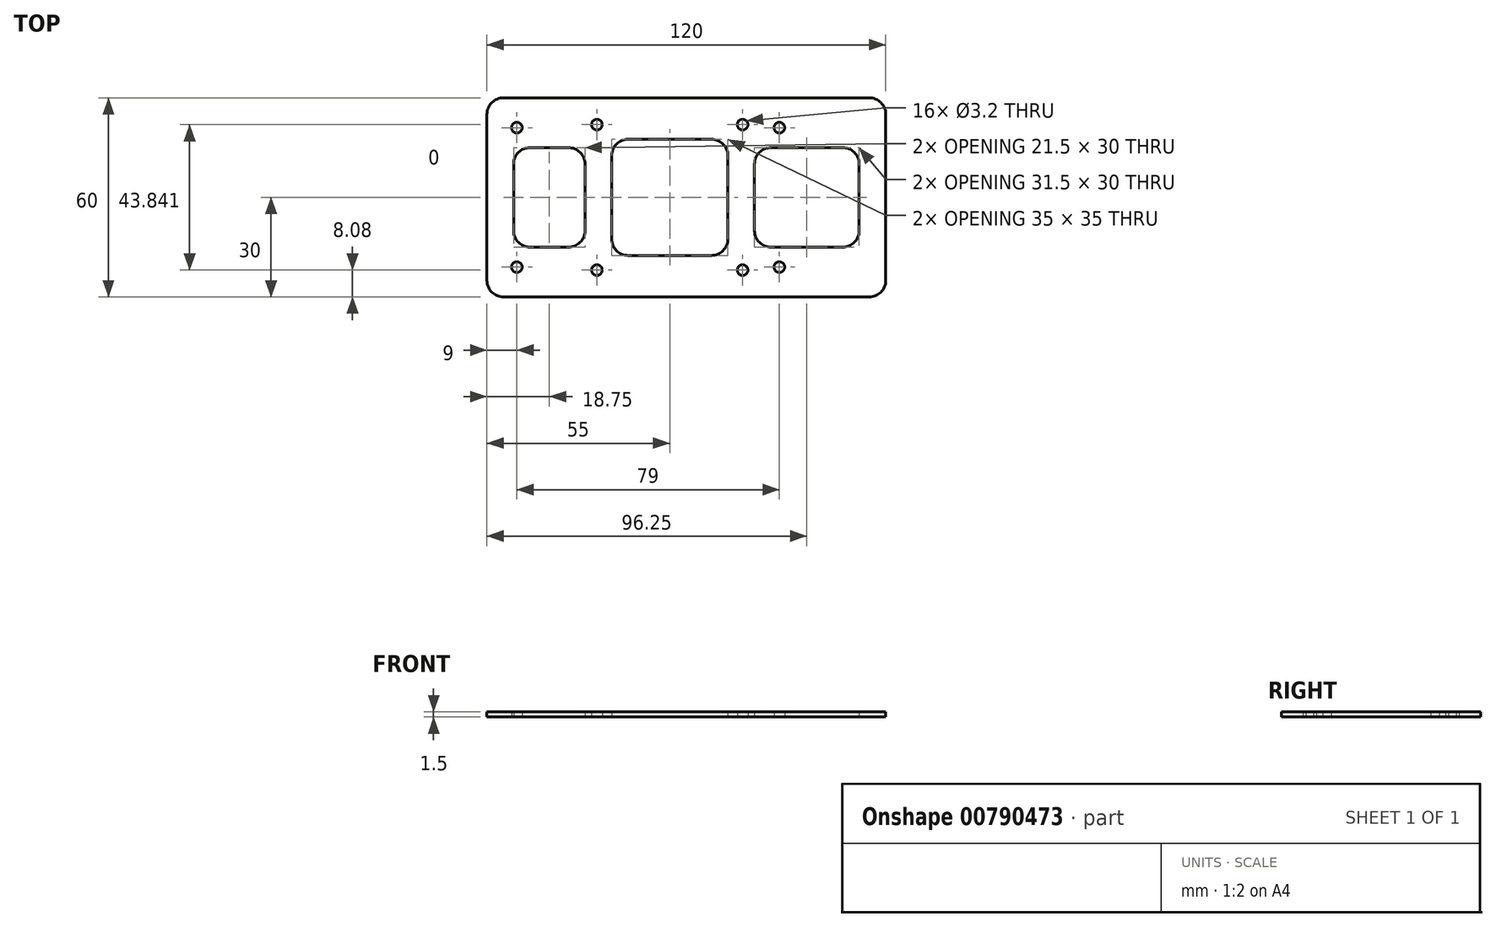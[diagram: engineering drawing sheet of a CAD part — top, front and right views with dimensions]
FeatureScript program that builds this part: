
annotation { "Feature Type Name" : "Feature", "Feature Type Description" : "" }
export const myFeature = defineFeature(function(context is Context, id is Id, definition is map)
    precondition{}
    {
        {
            var Q0;
            Q0=qCreatedBy(makeId("Top.planeOp"),FACE);
            var sketch = newSketch(context, id + "F0", { "sketchPlane" : qUnion([Q0])});
            skLineSegment(sketch, "E0.bottom", {"start": v(-60, 30) * mm, "end": v(60, 30) * mm});
            skLineSegment(sketch, "E0.top", {"start": v(-60, -30) * mm, "end": v(60, -30) * mm});
            skLineSegment(sketch, "E0.left", {"start": v(-60, 30) * mm, "end": v(-60, -30) * mm});
            skLineSegment(sketch, "E0.right", {"start": v(60, 30) * mm, "end": v(60, -30) * mm});
            skLineSegment(sketch, "E1.bottom", {"start": v(-51, 21) * mm, "end": v(28, 21) * mm, "construction": true});
            skLineSegment(sketch, "E1.top", {"start": v(-51, -21) * mm, "end": v(28, -21) * mm, "construction": true});
            skLineSegment(sketch, "E1.left", {"start": v(-51, 21) * mm, "end": v(-51, -21) * mm, "construction": true});
            skLineSegment(sketch, "E1.right", {"start": v(28, 21) * mm, "end": v(28, -21) * mm, "construction": true});
            skCircle(sketch, "E2", {"center": v(-51, 21) * mm, "radius": 1.6 * mm});
            skCircle(sketch, "E3", {"center": v(28, 21) * mm, "radius": 1.6 * mm});
            skCircle(sketch, "E4", {"center": v(-51, -21) * mm, "radius": 1.6 * mm});
            skCircle(sketch, "E5", {"center": v(28, -21) * mm, "radius": 1.6 * mm});
            skLineSegment(sketch, "E6.bottom", {"start": v(-26.92, 21.92) * mm, "end": v(16.92, 21.92) * mm, "construction": true});
            skLineSegment(sketch, "E6.top", {"start": v(-26.92, -21.92) * mm, "end": v(16.92, -21.92) * mm, "construction": true});
            skLineSegment(sketch, "E6.left", {"start": v(-26.92, 21.92) * mm, "end": v(-26.92, -21.92) * mm, "construction": true});
            skLineSegment(sketch, "E6.right", {"start": v(16.92, 21.92) * mm, "end": v(16.92, -21.92) * mm, "construction": true});
            skLineSegment(sketch, "E7", {"start": v(-26.92, -21.92) * mm, "end": v(16.92, 21.92) * mm, "construction": true});
            skCircle(sketch, "E8", {"center": v(16.92, 21.92) * mm, "radius": 1.6 * mm});
            skCircle(sketch, "E9", {"center": v(-26.92, 21.92) * mm, "radius": 1.6 * mm});
            skCircle(sketch, "E10", {"center": v(-26.92, -21.92) * mm, "radius": 1.6 * mm});
            skCircle(sketch, "E11", {"center": v(16.92, -21.92) * mm, "radius": 1.6 * mm});
            skLineSegment(sketch, "E12", {"start": v(-26.92, 21.92) * mm, "end": v(16.92, -21.92) * mm, "construction": true});
            skPoint(sketch, "E13", {"position": v(-5, 0) * mm});
            skLineSegment(sketch, "E14.bottom", {"start": v(-55, 25) * mm, "end": v(54.5, 25) * mm, "construction": true});
            skLineSegment(sketch, "E14.top", {"start": v(-55, -25) * mm, "end": v(54.5, -25) * mm, "construction": true});
            skLineSegment(sketch, "E14.left", {"start": v(-55, 25) * mm, "end": v(-55, -25) * mm, "construction": true});
            skLineSegment(sketch, "E14.right", {"start": v(54.5, 25) * mm, "end": v(54.5, -25) * mm, "construction": true});
            skLineSegment(sketch, "E15.bottom", {"start": v(-22.5, 17.5) * mm, "end": v(12.5, 17.5) * mm});
            skLineSegment(sketch, "E15.top", {"start": v(-22.5, -17.5) * mm, "end": v(12.5, -17.5) * mm});
            skLineSegment(sketch, "E15.left", {"start": v(-22.5, 17.5) * mm, "end": v(-22.5, -17.5) * mm});
            skLineSegment(sketch, "E15.right", {"start": v(12.5, 17.5) * mm, "end": v(12.5, -17.5) * mm});
            skLineSegment(sketch, "E16.bottom", {"start": v(52, -15) * mm, "end": v(20.5, -15) * mm});
            skLineSegment(sketch, "E16.top", {"start": v(52, 15) * mm, "end": v(20.5, 15) * mm});
            skLineSegment(sketch, "E16.left", {"start": v(52, -15) * mm, "end": v(52, 15) * mm});
            skLineSegment(sketch, "E16.right", {"start": v(20.5, -15) * mm, "end": v(20.5, 15) * mm});
            skPoint(sketch, "E16.middle", {"position": v(36.25, 0) * mm});
            skLineSegment(sketch, "E17.bottom", {"start": v(-52, -15) * mm, "end": v(-30.5, -15) * mm});
            skLineSegment(sketch, "E17.top", {"start": v(-52, 15) * mm, "end": v(-30.5, 15) * mm});
            skLineSegment(sketch, "E17.left", {"start": v(-52, -15) * mm, "end": v(-52, 15) * mm});
            skLineSegment(sketch, "E17.right", {"start": v(-30.5, -15) * mm, "end": v(-30.5, 15) * mm});
            skPoint(sketch, "E17.middle", {"position": v(-41.25, 0) * mm});
            skSolve(sketch);
        }
        {
            var Q0;
            Q0=makeQuery(id+"F0.imprint","IMPRINT",FACE,{"disambiguationData":[TD([[makeQuery(id+"F0.imprint","IMPRINT",EDGE,{"derivedFrom":sQuery(id+"F0.wireOp",EDGE,"E0.bottom")}),-1.0]])]});
            extrude(context, id + "F1", {"entities" : qUnion([Q0]), "depth" : 1.5 * mm, "offsetDistance" : 25 * mm});
        }
        {
            var Q0;
            Q0=makeQuery(id+"F1.opExtrude","SWEPT_EDGE",EDGE,{"disambiguationData":[OSD([sQuery(id+"F0.wireOp",EDGE,"E0.bottom"),sQuery(id+"F0.wireOp",EDGE,"E0.left")])]});
            var Q1;
            Q1=makeQuery(id+"F1.opExtrude","SWEPT_EDGE",EDGE,{"disambiguationData":[OSD([sQuery(id+"F0.wireOp",EDGE,"E0.top"),sQuery(id+"F0.wireOp",EDGE,"E0.left")])]});
            var Q2;
            Q2=makeQuery(id+"F1.opExtrude","SWEPT_EDGE",EDGE,{"disambiguationData":[OSD([sQuery(id+"F0.wireOp",EDGE,"E0.top"),sQuery(id+"F0.wireOp",EDGE,"E0.right")])]});
            var Q3;
            Q3=makeQuery(id+"F1.opExtrude","SWEPT_EDGE",EDGE,{"disambiguationData":[OSD([sQuery(id+"F0.wireOp",EDGE,"E0.bottom"),sQuery(id+"F0.wireOp",EDGE,"E0.right")])]});
            var Q4;
            Q4=makeQuery(id+"F1.opExtrude","SWEPT_EDGE",EDGE,{"disambiguationData":[OSD([sQuery(id+"F0.wireOp",EDGE,"E17.top"),sQuery(id+"F0.wireOp",EDGE,"E17.left")])]});
            var Q5;
            Q5=makeQuery(id+"F1.opExtrude","SWEPT_EDGE",EDGE,{"disambiguationData":[OSD([sQuery(id+"F0.wireOp",EDGE,"E17.top"),sQuery(id+"F0.wireOp",EDGE,"E17.right")])]});
            var Q6;
            Q6=makeQuery(id+"F1.opExtrude","SWEPT_EDGE",EDGE,{"disambiguationData":[OSD([sQuery(id+"F0.wireOp",EDGE,"E17.bottom"),sQuery(id+"F0.wireOp",EDGE,"E17.left")])]});
            var Q7;
            Q7=makeQuery(id+"F1.opExtrude","SWEPT_EDGE",EDGE,{"disambiguationData":[OSD([sQuery(id+"F0.wireOp",EDGE,"E17.bottom"),sQuery(id+"F0.wireOp",EDGE,"E17.right")])]});
            var Q8;
            Q8=makeQuery(id+"F1.opExtrude","SWEPT_EDGE",EDGE,{"disambiguationData":[OSD([sQuery(id+"F0.wireOp",EDGE,"E15.bottom"),sQuery(id+"F0.wireOp",EDGE,"E15.left")])]});
            var Q9;
            Q9=makeQuery(id+"F1.opExtrude","SWEPT_EDGE",EDGE,{"disambiguationData":[OSD([sQuery(id+"F0.wireOp",EDGE,"E15.bottom"),sQuery(id+"F0.wireOp",EDGE,"E15.right")])]});
            var Q10;
            Q10=makeQuery(id+"F1.opExtrude","SWEPT_EDGE",EDGE,{"disambiguationData":[OSD([sQuery(id+"F0.wireOp",EDGE,"E15.top"),sQuery(id+"F0.wireOp",EDGE,"E15.left")])]});
            var Q11;
            Q11=makeQuery(id+"F1.opExtrude","SWEPT_EDGE",EDGE,{"disambiguationData":[OSD([sQuery(id+"F0.wireOp",EDGE,"E15.top"),sQuery(id+"F0.wireOp",EDGE,"E15.right")])]});
            var Q12;
            Q12=makeQuery(id+"F1.opExtrude","SWEPT_EDGE",EDGE,{"disambiguationData":[OSD([sQuery(id+"F0.wireOp",EDGE,"E16.bottom"),sQuery(id+"F0.wireOp",EDGE,"E16.right")])]});
            var Q13;
            Q13=makeQuery(id+"F1.opExtrude","SWEPT_EDGE",EDGE,{"disambiguationData":[OSD([sQuery(id+"F0.wireOp",EDGE,"E16.bottom"),sQuery(id+"F0.wireOp",EDGE,"E16.left")])]});
            var Q14;
            Q14=makeQuery(id+"F1.opExtrude","SWEPT_EDGE",EDGE,{"disambiguationData":[OSD([sQuery(id+"F0.wireOp",EDGE,"E16.top"),sQuery(id+"F0.wireOp",EDGE,"E16.left")])]});
            var Q15;
            Q15=makeQuery(id+"F1.opExtrude","SWEPT_EDGE",EDGE,{"disambiguationData":[OSD([sQuery(id+"F0.wireOp",EDGE,"E16.top"),sQuery(id+"F0.wireOp",EDGE,"E16.right")])]});
            fillet(context, id + "F2", {"entities" : qUnion([Q0, Q1, Q2, Q3, Q4, Q5, Q6, Q7, Q8, Q9, Q10, Q11, Q12, Q13, Q14, Q15]), "radius" : 5 * mm, "tangentPropagation" : true, "allowEdgeOverflow" : false});
        }
        {
            var Q0;
            Q0=makeQuery(id+"F1.opExtrude","SWEPT_BODY",BODY,{"disambiguationData":[OSD([sQuery(id+"F0.wireOp",EDGE,"E0.bottom"),sQuery(id+"F0.wireOp",EDGE,"E0.top"),sQuery(id+"F0.wireOp",EDGE,"E0.left"),sQuery(id+"F0.wireOp",EDGE,"E0.right"),sQuery(id+"F0.wireOp",EDGE,"E2"),sQuery(id+"F0.wireOp",EDGE,"E3"),sQuery(id+"F0.wireOp",EDGE,"E4"),sQuery(id+"F0.wireOp",EDGE,"E5"),sQuery(id+"F0.wireOp",EDGE,"E8"),sQuery(id+"F0.wireOp",EDGE,"E9"),sQuery(id+"F0.wireOp",EDGE,"E10"),sQuery(id+"F0.wireOp",EDGE,"E11"),sQuery(id+"F0.wireOp",EDGE,"E15.bottom"),sQuery(id+"F0.wireOp",EDGE,"E15.top"),sQuery(id+"F0.wireOp",EDGE,"E15.left"),sQuery(id+"F0.wireOp",EDGE,"E15.right"),sQuery(id+"F0.wireOp",EDGE,"E16.bottom"),sQuery(id+"F0.wireOp",EDGE,"E16.top"),sQuery(id+"F0.wireOp",EDGE,"E16.left"),sQuery(id+"F0.wireOp",EDGE,"E16.right"),sQuery(id+"F0.wireOp",EDGE,"E17.bottom"),sQuery(id+"F0.wireOp",EDGE,"E17.top"),sQuery(id+"F0.wireOp",EDGE,"E17.left"),sQuery(id+"F0.wireOp",EDGE,"E17.right")])]});
            transform(context, id + "F3", {"entities" : qUnion([Q0]), "transformType" : TransformType.TRANSLATION_3D, "dx" : 0 * mm, "dy" : 0 * mm, "dz" : 0 * mm, "makeCopy" : true});
        }
    });
